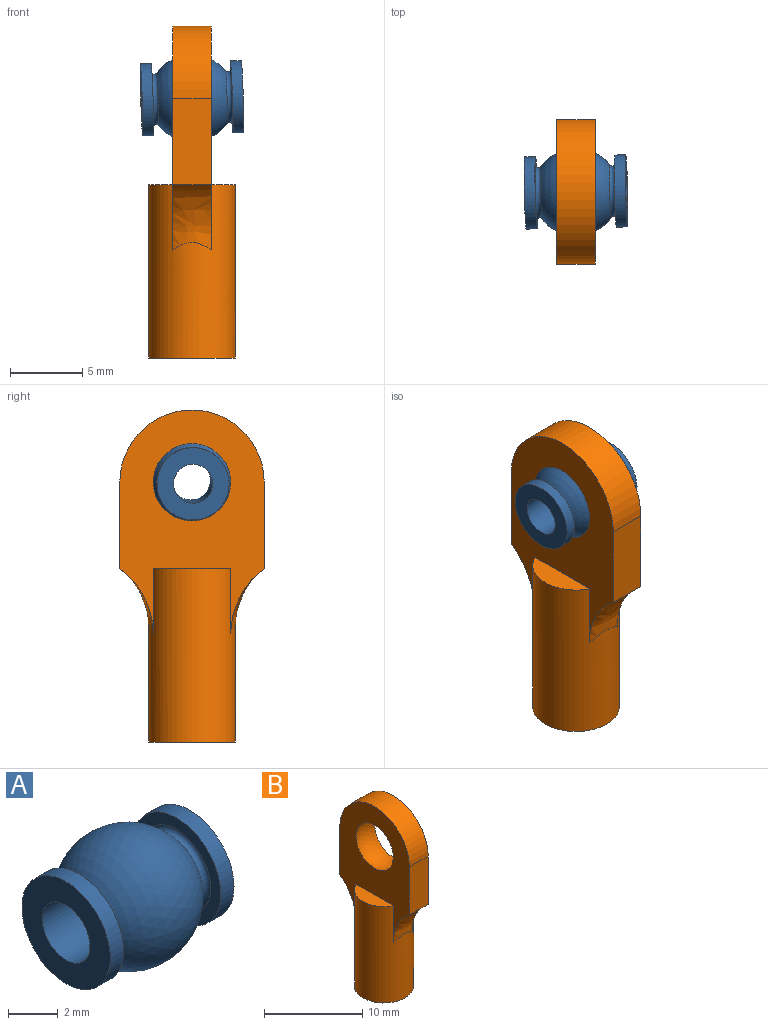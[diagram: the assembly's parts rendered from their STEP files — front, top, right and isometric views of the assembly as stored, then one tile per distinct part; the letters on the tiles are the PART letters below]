
ASSEMBLY  parts=2 mates=1
PART A: 10 faces, bbox 7x6x6 mm
  f0: plane 5x5mm, normal (1,0,0), area 13.9mm2, adj f1,f9
  f1: cylinder r=2.5mm len=5mm, axis (-1,0,0), area 11.8mm2, adj f0,f2
  f2: plane 5x5mm, normal (-1,0,0), area 7.9mm2, adj f1,f3
  f3: torus R=1.93mm, axis (-1,0,0), area 5.6mm2, adj f2,f4
  f4: sphere r=3mm, area 90.1mm2, adj f3,f5
  f5: torus R=1.93mm, axis (-1,0,0), area 5.6mm2, adj f4,f6
  f6: plane 5x5mm, normal (1,0,0), area 7.9mm2, adj f5,f7
  f7: cylinder r=2.5mm len=5mm, axis (-1,0,0), area 11.8mm2, adj f6,f8
  f8: plane 5x5mm, normal (-1,0,0), area 13.9mm2, adj f7,f9
  f9: cylinder r=1.35mm len=7mm, axis (-1,0,0), area 59.4mm2, adj f0,f8
PART B: 14 faces, bbox 9.4x10.6x23.6 mm
  f0: plane 16.16x10.65mm, normal (1,0,0), area 83mm2, adj f2,f3,f4,f5,f6,f8,f11,f12
  f1: plane 16.16x10.65mm, normal (-1,0,0), area 83mm2, adj f2,f3,f4,f5,f8,f10,f11,f12
  f2: plane 6.01x2.71mm, normal (0,1,0), area 16.2mm2, adj f0,f1,f3,f12
  f3: cylinder r=5mm len=10mm, axis (-1,0,0), area 42.4mm2, adj f0,f1,f2,f4
  f4: plane 6.01x2.71mm, normal (0,-1,0), area 16.2mm2, adj f0,f1,f3,f11
  f5: sphere r=3mm, area 50.9mm2, adj f0,f1
  f6: plane 5.36x1.65mm, normal (0,0,1), area 6.3mm2, adj f0,f8
  f7: cylinder r=1.5mm len=11mm, axis (0,0,1), area 103.7mm2, adj f9,f13
  f8: cylinder r=3mm len=12mm, axis (0,0,1), area 200.9mm2, adj f0,f1,f6,f9,f10,f11,f12
  f9: plane 6x6mm, normal (0,0,-1), area 21.2mm2, adj f7,f8
  f10: plane 5.36x1.65mm, normal (0,0,1), area 6.3mm2, adj f1,f8
  f11: bspline ~8.44x4.7mm, area 14.9mm2, adj f0,f1,f4,f8
  f12: bspline ~8.44x4.7mm, area 14.9mm2, adj f0,f1,f2,f8
  f13: plane 3x3mm, normal (0,0,-1), area 7.1mm2, adj f7
PLACE A rot(axis=(0.43,-0.75,0.5),2.5deg) t=(0,0,0)mm
PLACE B at identity fixed
MATE ball A.f4 <-> B.f8  axis (-0.03,-0.02,1) through (0,0,0)mm
